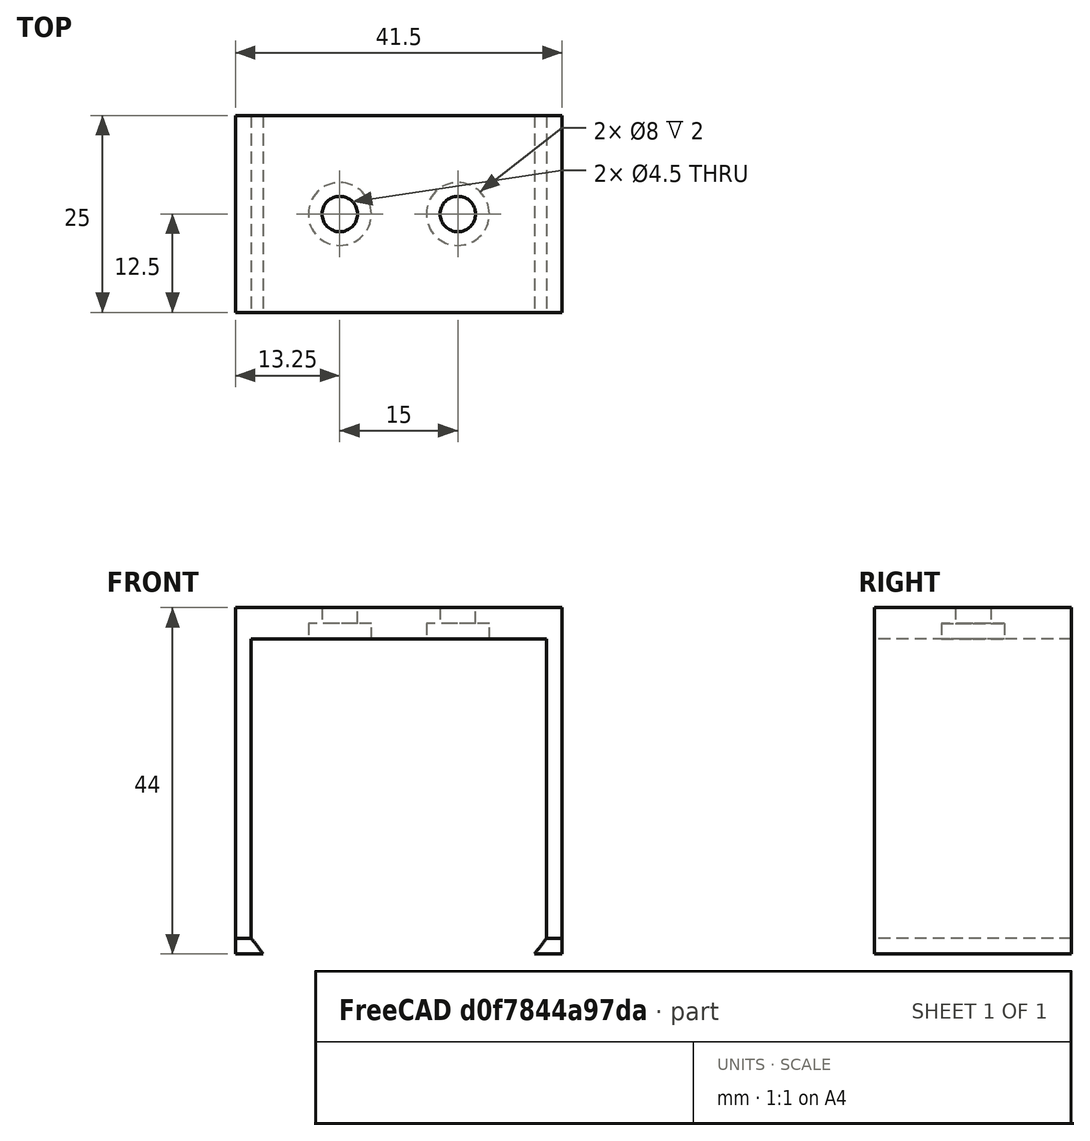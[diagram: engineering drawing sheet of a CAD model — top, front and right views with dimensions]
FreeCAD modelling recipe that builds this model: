
FCSTD DOCUMENT  (FreeCAD 0.21R33771 (Git))
Label: Syme Z4W Wall Mount
License: All rights reserved
LicenseURL: http://en.wikipedia.org/wiki/All_rights_reserved
objects: Sketcher::SketchObject×5, PartDesign::Pad×2, PartDesign::Pocket×2, PartDesign::AdditiveLoft×1, PartDesign::Mirrored×1, PartDesign::Body×1, Mesh::Feature×1
note: 17 computed .brp shape members not serialized (recipe doc carries the construction recipe); baked Part::Feature solids carry a one-line shape summary decoded from their .brp

FEATURE [Sketcher::SketchObject] Sketch  label="BaseSketch"
  FullyConstrained = true
  MapMode = 5
  Support = -> [XY_Plane]
  expr: Constraints[11] = 37.5 + 2 + 2
  sketch-geometry (5):
    g0: LineSegment StartX=20.75 StartY=-12.5 StartZ=0 EndX=20.75 EndY=12.5 EndZ=0
    g1: LineSegment StartX=20.75 StartY=12.5 StartZ=0 EndX=-20.75 EndY=12.5 EndZ=0
    g2: LineSegment StartX=-20.75 StartY=12.5 StartZ=0 EndX=-20.75 EndY=-12.5 EndZ=0
    g3: LineSegment StartX=-20.75 StartY=-12.5 StartZ=0 EndX=20.75 EndY=-12.5 EndZ=0
    g4: GeomPoint X=0 Y=0 Z=0
  constraints (12):
    c: Coincident(g0,g1)
    c: Coincident(g1,g2)
    c: Coincident(g2,g3)
    c: Coincident(g3,g0)
    c: Horizontal(g1)
    c: Horizontal(g3)
    c: Vertical(g0)
    c: Vertical(g2)
    c: Symmetric(g1,g0,g4)
    c: Coincident(g4,g-1)
    c: DistanceY(g2,g1) = 25
    c: DistanceX(g2,g0) = 41.5
FEATURE [PartDesign::Pad] Pad
  Direction = (0,0,1)
  Length = 4
  Length2 = 10
  Profile = -> Sketch
  ReferenceAxis = -> Sketch [N_Axis]
  Type = 0
FEATURE [Sketcher::SketchObject] Sketch001  label="SkrewHoleSketch"
  FullyConstrained = true
  MapMode = 5
  Support = -> [XY_Plane]
  sketch-geometry (2):
    g0: Circle CenterX=-7.5 CenterY=0 CenterZ=0 NormalX=0 NormalY=0 NormalZ=1 AngleXU=0 Radius=2.25
    g1: Circle CenterX=7.5 CenterY=0 CenterZ=0 NormalX=0 NormalY=0 NormalZ=1 AngleXU=0 Radius=2.25
  constraints (5):
    c: PointOnObject(g0,g-1)
    c: Symmetric(g0,g1,g-1)
    c: DistanceX(g0,g1) = 15  'centerOffset'
    c: Equal(g0,g1)
    c: Diameter(g0) = 4.5
FEATURE [PartDesign::Pocket] Pocket  label="SkrewHole"
  BaseFeature = -> Pad
  Direction = (0,0,-1)
  Length = 4
  Length2 = 5
  Profile = -> Sketch001
  ReferenceAxis = -> Sketch001 [N_Axis]
  Reversed = true
  Type = 0
FEATURE [Sketcher::SketchObject] Sketch002  label="SkrewBrimSketch"
  FullyConstrained = true
  MapMode = 5
  Support = -> [XY_Plane]
  expr: Constraints[2] = <<SkrewHoleSketch>>.Constraints.centerOffset
  sketch-geometry (2):
    g0: Circle CenterX=-7.5 CenterY=0 CenterZ=0 NormalX=0 NormalY=0 NormalZ=1 AngleXU=0 Radius=4
    g1: Circle CenterX=7.5 CenterY=0 CenterZ=0 NormalX=0 NormalY=0 NormalZ=1 AngleXU=0 Radius=4
  constraints (5):
    c: PointOnObject(g0,g-1)
    c: Symmetric(g0,g1,g-2)
    c: DistanceX(g0,g1) = 15
    c: Equal(g0,g1)
    c: Diameter(g0) = 8
FEATURE [PartDesign::Pocket] Pocket001  label="SkrewBrim"
  BaseFeature = -> Pocket
  Direction = (0,0,-1)
  Length = 2
  Length2 = 5
  Profile = -> Sketch002
  ReferenceAxis = -> Sketch002 [N_Axis]
  Reversed = true
  Type = 0
FEATURE [Sketcher::SketchObject] Sketch003
  ExternalGeometry = -> [Pocket001]
  FullyConstrained = true
  MapMode = 5
  Support = -> [XY_Plane]
  sketch-geometry (4):
    g0: LineSegment StartX=-20.75 StartY=12.5 StartZ=0 EndX=-18.75 EndY=12.5 EndZ=0
    g1: LineSegment StartX=-18.75 StartY=12.5 StartZ=0 EndX=-18.75 EndY=-12.5 EndZ=0
    g2: LineSegment StartX=-18.75 StartY=-12.5 StartZ=0 EndX=-20.75 EndY=-12.5 EndZ=0
    g3: LineSegment StartX=-20.75 StartY=-12.5 StartZ=0 EndX=-20.75 EndY=12.5 EndZ=0
  constraints (10):
    c: Coincident(g0,g1)
    c: Coincident(g1,g2)
    c: Coincident(g2,g3)
    c: Coincident(g3,g0)
    c: Horizontal(g0)
    c: Horizontal(g2)
    c: Vertical(g1)
    c: Coincident(g2,g-4)
    c: DistanceX(g0,g0) = 2
    c: Coincident(g0,g-3)
FEATURE [PartDesign::Pad] Pad001
  BaseFeature = -> Pocket001
  Direction = (0,0,1)
  Length = 38
  Length2 = 10
  Profile = -> Sketch003
  ReferenceAxis = -> Sketch003 [N_Axis]
  Reversed = true
  Type = 0
FEATURE [Sketcher::SketchObject] Sketch004
  AttachmentOffset = pos=(0,0,-40) rot=(0,0,1;0rad)
  ExternalGeometry = -> [Pad001]
  FullyConstrained = true
  MapMode = 5
  Placement = pos=(0,0,-40) rot=(0,0,1;0rad)
  Support = -> [XY_Plane]
  sketch-geometry (4):
    g0: LineSegment StartX=-20.75 StartY=12.5 StartZ=0 EndX=-17.25 EndY=12.5 EndZ=0
    g1: LineSegment StartX=-17.25 StartY=12.5 StartZ=0 EndX=-17.25 EndY=-12.5 EndZ=0
    g2: LineSegment StartX=-17.25 StartY=-12.5 StartZ=0 EndX=-20.75 EndY=-12.5 EndZ=0
    g3: LineSegment StartX=-20.75 StartY=-12.5 StartZ=0 EndX=-20.75 EndY=12.5 EndZ=0
  constraints (10):
    c: Coincident(g0,g1)
    c: Coincident(g1,g2)
    c: Coincident(g2,g3)
    c: Coincident(g3,g0)
    c: Horizontal(g0)
    c: Horizontal(g2)
    c: Vertical(g1)
    c: Coincident(g0,g-3)
    c: Coincident(g-4,g2)
    c: DistanceX(g0,g0) = 3.5
FEATURE [PartDesign::AdditiveLoft] AdditiveLoft
  BaseFeature = -> Pad001
  Closed = false
  Profile = -> Pad001 [Face15]
  Ruled = false
  Sections = -> [Sketch004]
FEATURE [PartDesign::Mirrored] Mirrored
  BaseFeature = -> AdditiveLoft
  MirrorPlane = -> YZ_Plane
  Originals = -> [AdditiveLoft,Pad001]
FEATURE [PartDesign::Body] Body
  Group = -> [Sketch,Pad,Sketch001,Pocket,Sketch002,Pocket001,Sketch003,Pad001,Sketch004,AdditiveLoft,Mirrored]
  Origin = -> Origin
  Tip = -> Mirrored
FEATURE [Mesh::Feature] Mesh  label="Mirrored (Meshed)"
